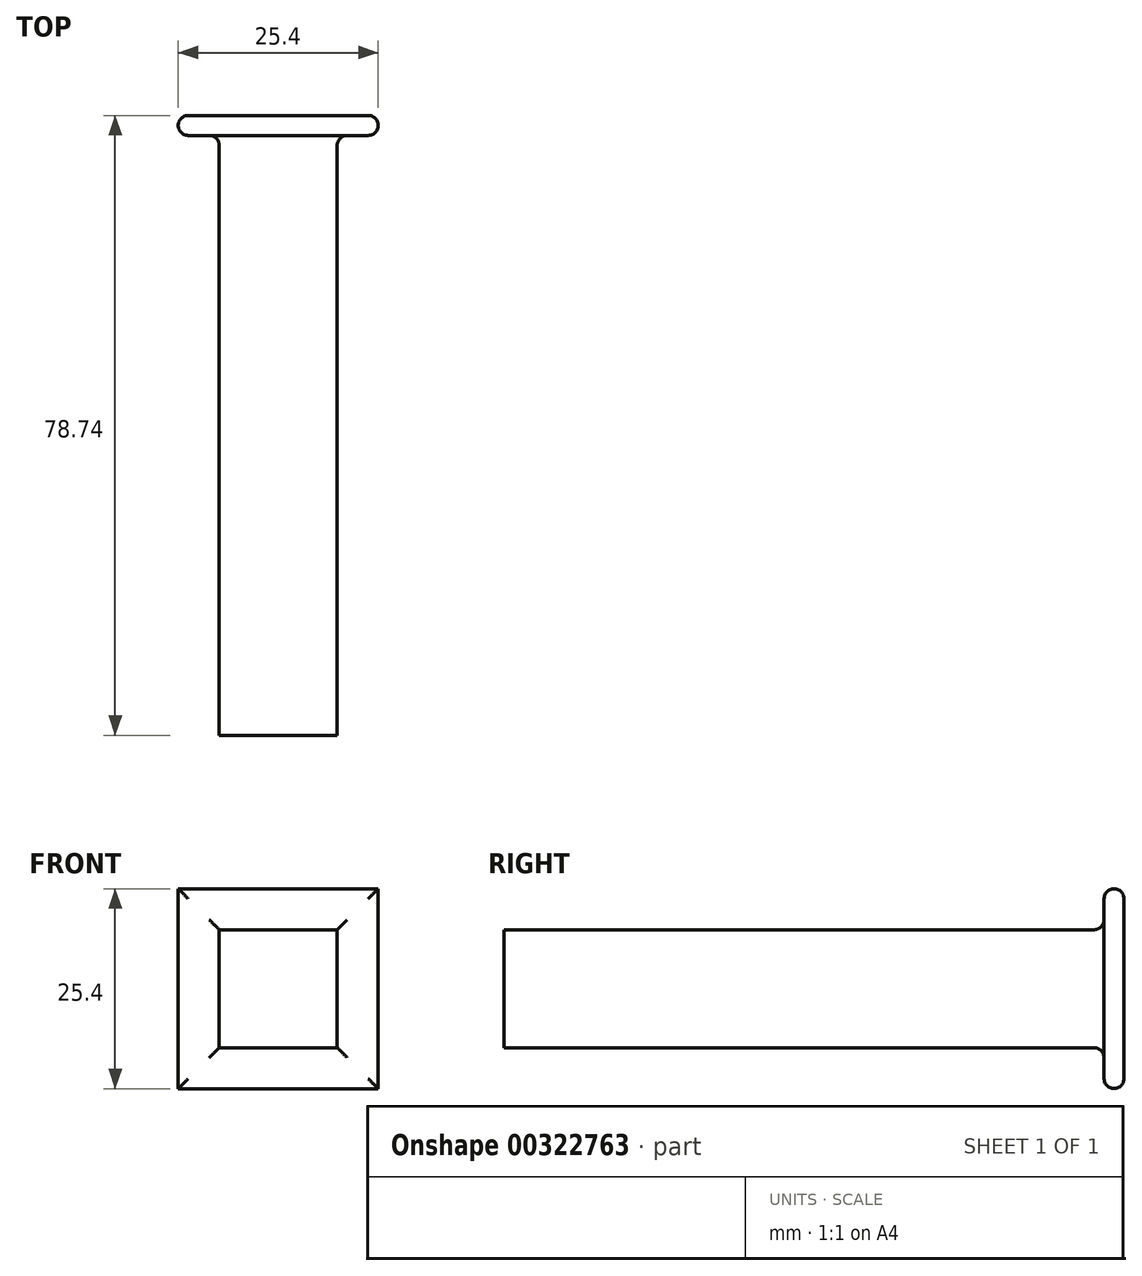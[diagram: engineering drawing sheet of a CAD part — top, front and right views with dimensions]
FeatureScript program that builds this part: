
annotation { "Feature Type Name" : "Feature", "Feature Type Description" : "" }
export const myFeature = defineFeature(function(context is Context, id is Id, definition is map)
    precondition{}
    {
        {
            var Q0;
            Q0=qCreatedBy(makeId("Front.planeOp"),FACE);
            var sketch = newSketch(context, id + "F0", { "sketchPlane" : qUnion([Q0])});
            skLineSegment(sketch, "E0.bottom", {"start": v(-12.7, 12.7) * mm, "end": v(12.7, 12.7) * mm});
            skLineSegment(sketch, "E0.top", {"start": v(-12.7, -12.7) * mm, "end": v(12.7, -12.7) * mm});
            skLineSegment(sketch, "E0.left", {"start": v(-12.7, 12.7) * mm, "end": v(-12.7, -12.7) * mm});
            skLineSegment(sketch, "E0.right", {"start": v(12.7, 12.7) * mm, "end": v(12.7, -12.7) * mm});
            skSolve(sketch);
        }
        {
            var Q0;
            Q0=makeQuery(id+"F0.imprint","IMPRINT",FACE,{"disambiguationData":[TD([[makeQuery(id+"F0.imprint","IMPRINT",EDGE,{"derivedFrom":sQuery(id+"F0.wireOp",EDGE,"E0.bottom")}),-1.0]])]});
            extrude(context, id + "F1", {"entities" : qUnion([Q0]), "depth" : 2.54 * mm});
        }
        {
            var Q0;
            Q0=makeQuery(id+"F1.opExtrude","CAP_FACE",FACE,{"disambiguationData":[OSD([sQuery(id+"F0.wireOp",EDGE,"E0.bottom"),sQuery(id+"F0.wireOp",EDGE,"E0.top"),sQuery(id+"F0.wireOp",EDGE,"E0.left"),sQuery(id+"F0.wireOp",EDGE,"E0.right")])],"isStart":false});
            var sketch = newSketch(context, id + "F2", { "sketchPlane" : qUnion([Q0])});
            skLineSegment(sketch, "E1.bottom", {"start": v(-7.5, 7.5) * mm, "end": v(7.5, 7.5) * mm});
            skLineSegment(sketch, "E1.top", {"start": v(-7.5, -7.5) * mm, "end": v(7.5, -7.5) * mm});
            skLineSegment(sketch, "E1.left", {"start": v(-7.5, 7.5) * mm, "end": v(-7.5, -7.5) * mm});
            skLineSegment(sketch, "E1.right", {"start": v(7.5, 7.5) * mm, "end": v(7.5, -7.5) * mm});
            skSolve(sketch);
        }
        {
            var Q0;
            Q0=makeQuery(id+"F2.imprint","IMPRINT",FACE,{"disambiguationData":[TD([[makeQuery(id+"F2.imprint","IMPRINT",EDGE,{"derivedFrom":sQuery(id+"F2.wireOp",EDGE,"E1.bottom")}),-1.0]])]});
            extrude(context, id + "F3", {"entities" : qUnion([Q0]), "operationType" : NewBodyOperationType.ADD, "depth" : 76.2 * mm});
        }
        {
            var Q0;
            Q0=makeQuery(id+"F1.opExtrude","CAP_FACE",FACE,{"disambiguationData":[OSD([sQuery(id+"F0.wireOp",EDGE,"E0.bottom"),sQuery(id+"F0.wireOp",EDGE,"E0.top"),sQuery(id+"F0.wireOp",EDGE,"E0.left"),sQuery(id+"F0.wireOp",EDGE,"E0.right")])],"isStart":true});
            var Q1;
            Q1=makeQuery(id+"F1.opExtrude","CAP_FACE",FACE,{"disambiguationData":[OSD([sQuery(id+"F0.wireOp",EDGE,"E0.bottom"),sQuery(id+"F0.wireOp",EDGE,"E0.top"),sQuery(id+"F0.wireOp",EDGE,"E0.left"),sQuery(id+"F0.wireOp",EDGE,"E0.right")])],"isStart":false});
            fillet(context, id + "F4", {"entities" : qUnion([Q0, Q1]), "radius" : 1.27 * mm, "tangentPropagation" : true, "allowEdgeOverflow" : false});
        }
    });
